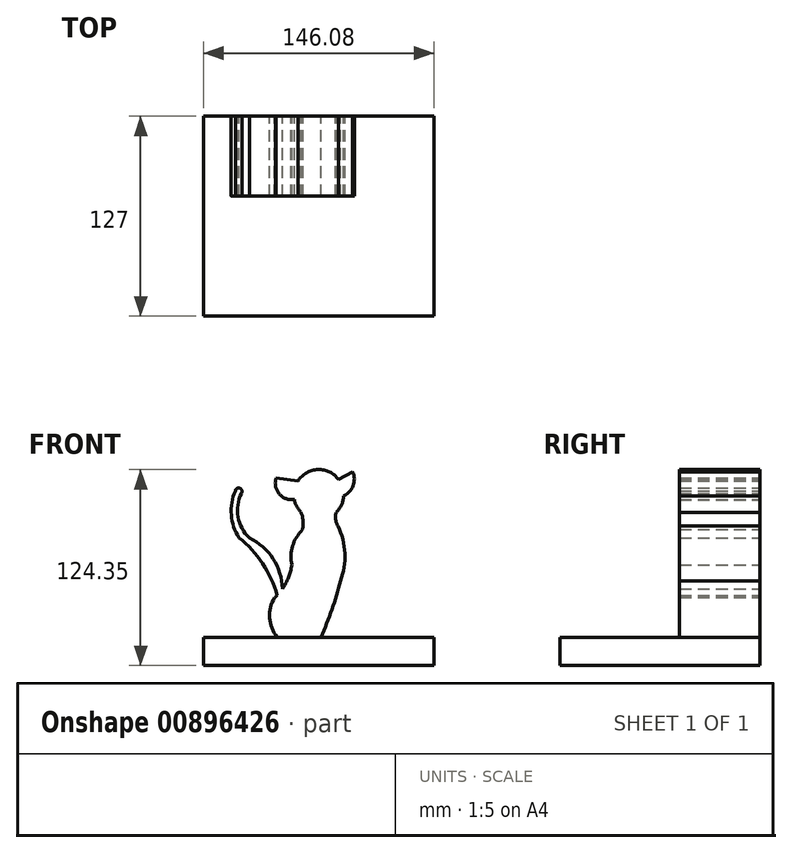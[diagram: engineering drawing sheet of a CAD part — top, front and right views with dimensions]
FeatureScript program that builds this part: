
annotation { "Feature Type Name" : "Feature", "Feature Type Description" : "" }
export const myFeature = defineFeature(function(context is Context, id is Id, definition is map)
    precondition{}
    {
        {
            var Q0;
            Q0=qCreatedBy(makeId("Front.planeOp"),FACE);
            var sketch = newSketch(context, id + "F0", { "sketchPlane" : qUnion([Q0])});
            skLineSegment(sketch, "E0.bottom", {"start": v(-73.04, -57.22) * mm, "end": v(73.04, -57.22) * mm});
            skLineSegment(sketch, "E0.top", {"start": v(-73.04, -75.06) * mm, "end": v(73.04, -75.06) * mm});
            skLineSegment(sketch, "E0.left", {"start": v(-73.04, -57.22) * mm, "end": v(-73.04, -75.06) * mm});
            skLineSegment(sketch, "E0.right", {"start": v(73.04, -57.22) * mm, "end": v(73.04, -75.06) * mm});
            skArc(sketch, "E1", {"start": v(10.92, 21.94) * mm, "mid": v(0.34, 49.29) * mm, "end": v(-11.4, 22.43) * mm});
            skPoint(sketch, "E2.start.orphan", {"position": v(-12.04, 9.46) * mm});
            skPoint(sketch, "E3.end.orphan", {"position": v(12.05, 9.45) * mm});
            skPoint(sketch, "E3.start.orphan", {"position": v(12.05, 23.13) * mm});
            skPoint(sketch, "E4.MirrorCS.start.orphan", {"position": v(12.04, 9.46) * mm});
            skPoint(sketch, "E5.start.orphan", {"position": v(26.55, -23.68) * mm});
            skPoint(sketch, "E6.start.orphan", {"position": v(-26.55, -23.68) * mm});
            skArc(sketch, "E7", {"start": v(15.56, -15.73) * mm, "mid": v(16.2, -13.16) * mm, "end": v(16.43, -10.52) * mm});
            skArc(sketch, "E8", {"start": v(-10.3, 11.12) * mm, "mid": v(-9.96, 16.86) * mm, "end": v(-11.4, 22.43) * mm});
            skArc(sketch, "E9", {"start": v(10.92, 21.94) * mm, "mid": v(10.78, 17.57) * mm, "end": v(12.1, 13.4) * mm});
            skArc(sketch, "E10", {"start": v(13.82, -21.43) * mm, "mid": v(16.62, -3.83) * mm, "end": v(12.1, 13.4) * mm});
            skArc(sketch, "E11", {"start": v(-10.3, 11.12) * mm, "mid": v(-16.64, 0.77) * mm, "end": v(-17.13, -11.34) * mm});
            skArc(sketch, "E12", {"start": v(1.4, -57.22) * mm, "mid": v(8.39, -39.6) * mm, "end": v(13.82, -21.43) * mm});
            skArc(sketch, "E13", {"start": v(-27.68, -31.8) * mm, "mid": v(-20.67, -22.46) * mm, "end": v(-17.13, -11.34) * mm});
            skArc(sketch, "E14", {"start": v(-28.04, -31.9) * mm, "mid": v(-31.2, -44.8) * mm, "end": v(-26.44, -57.22) * mm});
            skArc(sketch, "E15", {"start": v(-27.68, -31.8) * mm, "mid": v(-27.88, -31.8) * mm, "end": v(-28.04, -31.9) * mm});
            skLineSegment(sketch, "E16", {"start": v(12.67, 42.97) * mm, "end": v(21.57, 47.89) * mm});
            skLineSegment(sketch, "E17", {"start": v(-13.23, 42.17) * mm, "end": v(-27.04, 44.1) * mm});
            skArc(sketch, "E18", {"start": v(-27.04, 44.1) * mm, "mid": v(-25.19, 33.95) * mm, "end": v(-15.54, 30.28) * mm});
            skArc(sketch, "E19", {"start": v(15.83, 32.53) * mm, "mid": v(21.83, 39.04) * mm, "end": v(21.57, 47.89) * mm});
            skArc(sketch, "E20", {"start": v(-23.14, -26.55) * mm, "mid": v(-29, -7.36) * mm, "end": v(-44.04, 5.93) * mm});
            skArc(sketch, "E21", {"start": v(-26.42, -30.53) * mm, "mid": v(-35.64, -10.39) * mm, "end": v(-50.63, 5.93) * mm});
            skArc(sketch, "E22", {"start": v(-52.96, 35.77) * mm, "mid": v(-55.55, 20.56) * mm, "end": v(-50.63, 5.93) * mm});
            skArc(sketch, "E23", {"start": v(-49.12, 34.27) * mm, "mid": v(-51.28, 19.26) * mm, "end": v(-44.04, 5.93) * mm});
            skArc(sketch, "E24", {"start": v(-49.12, 34.27) * mm, "mid": v(-50.1, 37.45) * mm, "end": v(-52.96, 35.77) * mm});
            skSolve(sketch);
        }
        {
            var Q0;
            Q0=makeQuery(id+"F0.imprint","IMPRINT",FACE,{"disambiguationData":[TD([[makeQuery(id+"F0.imprint","IMPRINT",EDGE,{"derivedFrom":sQuery(id+"F0.wireOp",EDGE,"E0.top")}),1.0]])]});
            extrude(context, id + "F1", {"entities" : qUnion([Q0]), "depth" : 127 * mm, "offsetDistance" : 25.4 * mm});
        }
        {
            var Q0;
            {var subQ6=sQuery(id+"F0.wireOp",EDGE,"E8");Q0=makeQuery(id+"F0.imprint","IMPRINT",FACE,{"disambiguationData":[TD([[makeQuery(id+"F0.imprint","IMPRINT",EDGE,{"derivedFrom":subQ6}),-1.0]])]});}
            var Q1;
            {var subQ0=sQuery(id+"F0.wireOp",EDGE,"E16");Q1=makeQuery(id+"F0.imprint","IMPRINT",FACE,{"disambiguationData":[TD([[makeQuery(id+"F0.imprint","IMPRINT",EDGE,{"derivedFrom":subQ0}),-1.0]])]});}
            var Q2;
            {var subQ0=sQuery(id+"F0.wireOp",EDGE,"E17");Q2=makeQuery(id+"F0.imprint","IMPRINT",FACE,{"disambiguationData":[TD([[makeQuery(id+"F0.imprint","IMPRINT",EDGE,{"derivedFrom":subQ0}),1.0]])]});}
            var Q3;
            {var subQ1=sQuery(id+"F0.wireOp",EDGE,"E20");Q3=makeQuery(id+"F0.imprint","IMPRINT",FACE,{"disambiguationData":[TD([[makeQuery(id+"F0.imprint","IMPRINT",EDGE,{"derivedFrom":subQ1}),1.0]])]});}
            extrude(context, id + "F2", {"entities" : qUnion([Q0, Q1, Q2, Q3]), "operationType" : NewBodyOperationType.ADD, "depth" : 50.8 * mm, "offsetDistance" : 25.4 * mm});
        }
    });
